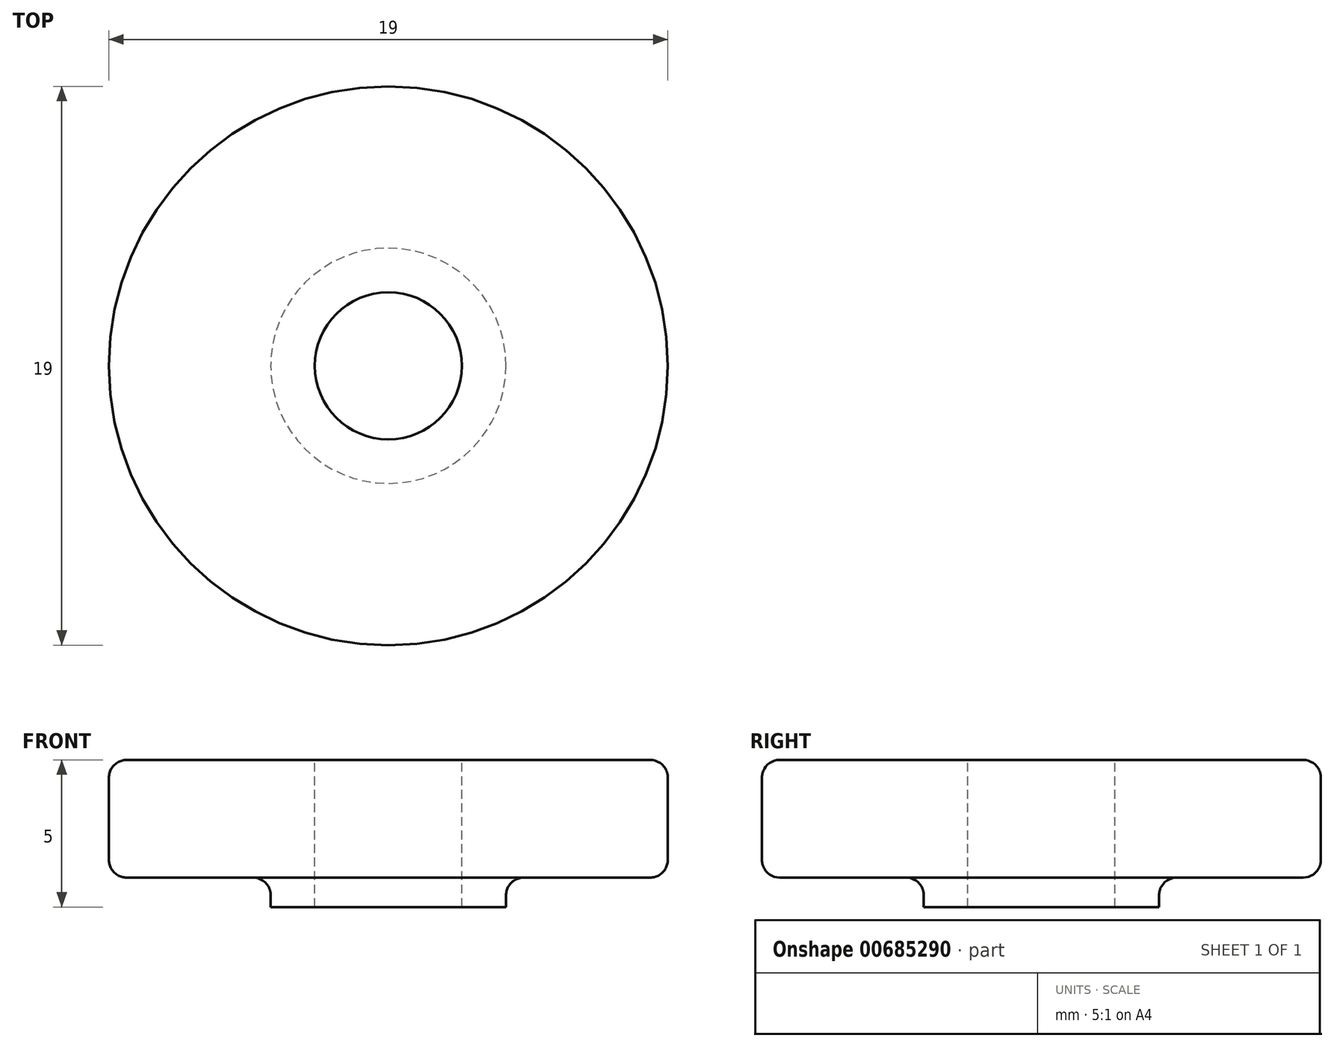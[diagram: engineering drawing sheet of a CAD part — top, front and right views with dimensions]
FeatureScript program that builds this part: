
annotation { "Feature Type Name" : "Feature", "Feature Type Description" : "" }
export const myFeature = defineFeature(function(context is Context, id is Id, definition is map)
    precondition{}
    {
        {
            var Q0;
            Q0=qCreatedBy(makeId("Front.planeOp"),FACE);
            var sketch = newSketch(context, id + "F0", { "sketchPlane" : qUnion([Q0])});
            skLineSegment(sketch, "E0", {"start": v(0, 0) * mm, "end": v(-4, 0) * mm});
            skLineSegment(sketch, "E1", {"start": v(-4, 0) * mm, "end": v(-4, 1) * mm});
            skLineSegment(sketch, "E2", {"start": v(-4, 1) * mm, "end": v(-9.5, 1) * mm});
            skLineSegment(sketch, "E3", {"start": v(-9.5, 1) * mm, "end": v(-9.5, 5) * mm});
            skLineSegment(sketch, "E4", {"start": v(-9.5, 5) * mm, "end": v(0, 5) * mm});
            skLineSegment(sketch, "E5", {"start": v(0, 5) * mm, "end": v(0, 0) * mm});
            skSolve(sketch);
        }
        {
            var Q0;
            Q0=makeQuery(id+"F0.imprint","IMPRINT",FACE,{"disambiguationData":[TD([[makeQuery(id+"F0.imprint","IMPRINT",EDGE,{"derivedFrom":sQuery(id+"F0.wireOp",EDGE,"E0")}),-1.0]])]});
            var Q1;
            Q1=sQuery(id+"F0.wireOp",EDGE,"E5");
            revolve(context, id + "F1", {"entities" : qUnion([Q0]), "axis" : qUnion([Q1]), "revolveType" : RevolveType.FULL});
        }
        {
            var Q0;
            Q0=makeQuery(id+"F1.opRevolve","SWEPT_FACE",FACE,{"disambiguationData":[OSD([sQuery(id+"F0.wireOp",EDGE,"E4")])]});
            var sketch = newSketch(context, id + "F2", { "sketchPlane" : qUnion([Q0])});
            skCircle(sketch, "E6", {"center": v(0, 0) * mm, "radius": 2.5 * mm});
            skSolve(sketch);
        }
        {
            var Q0;
            Q0=makeQuery(id+"F2.imprint","IMPRINT",FACE,{"disambiguationData":[TD([[makeQuery(id+"F2.imprint","IMPRINT",EDGE,{"derivedFrom":sQuery(id+"F2.wireOp",EDGE,"E6")}),1.0]])]});
            extrude(context, id + "F3", {"entities" : qUnion([Q0]), "operationType" : NewBodyOperationType.REMOVE, "oppositeDirection" : true, "depth" : 11.3 * mm, "offsetDistance" : 25 * mm});
        }
        {
            var Q0;
            Q0=makeQuery(id+"F1.opRevolve","SWEPT_EDGE",EDGE,{"disambiguationData":[OSD([sQuery(id+"F0.wireOp",EDGE,"E3"),sQuery(id+"F0.wireOp",EDGE,"E4")])]});
            var Q1;
            Q1=makeQuery(id+"F1.opRevolve","SWEPT_EDGE",EDGE,{"disambiguationData":[OSD([sQuery(id+"F0.wireOp",EDGE,"E2"),sQuery(id+"F0.wireOp",EDGE,"E3")])]});
            var Q2;
            Q2=makeQuery(id+"F1.opRevolve","SWEPT_EDGE",EDGE,{"disambiguationData":[OSD([sQuery(id+"F0.wireOp",EDGE,"E1"),sQuery(id+"F0.wireOp",EDGE,"E2")])]});
            fillet(context, id + "F4", {"entities" : qUnion([Q0, Q1, Q2]), "tangentPropagation" : true, "radius" : 0.6 * mm, "defaultsChanged" : false, "vertexSettings" : [], "allowEdgeOverflow" : false});
        }
    });
